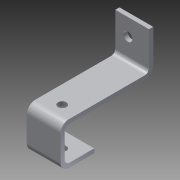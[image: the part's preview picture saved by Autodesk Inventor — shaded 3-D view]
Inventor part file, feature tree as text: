
AUTODESK INVENTOR PART (.ipt)
format: ipt  version: 2013 (Build 170138000, 138)  size: 136,704 bytes
history: native  units: in
note: dims shown in document units (in); Inventor stores cm internally (conversion verified against a paired STEP export)
features: sheet_metal_op x10, sketch x5, other x4, extrude x1, reference x1
ambient origin geometry x8: Origin, YZ Plane, XZ Plane, XY Plane, X Axis, Y Axis, Z Axis, Center Point
bodies: Solid1 (feature_tree)
feature tree (21):
  sheet_metal_op  "Face1"
  sheet_metal_op  "Flange1"
  sheet_metal_op  "Flange2"
  sheet_metal_op  "Flange3"
  extrude  "Extrusion1"  Depth=0.125in
  sketch  "Sketch1"  dims[d0=0.125in d1=0.125in]
  other  "Plate1"
  sketch  "Sketch2"  dims[d2=0.0625in]
  other  "Plate2"
  sheet_metal_op  "Bend1"
  sheet_metal_op  "Corner1"
  sketch  "Sketch3"  dims[d3=0.25in]
  other  "Plate3"
  sheet_metal_op  "Bend2"
  sheet_metal_op  "Corner2"
  sketch  "Sketch4"  dims[d4=0.125in]
  other  "Plate4"
  sheet_metal_op  "Bend3"
  sheet_metal_op  "Corner3"
  sketch  "Sketch5"  dims[d5=2.5in d6=90.0deg d7=0.125in d8=0.5in d9=0.125in d10=0.125in d11=0.125in d12=0.0625in d13=0.25in d14=0.125in d15=1.0in d16=90.0deg d17=0.125in d18=0.5in d19=0.125in d20=0.125in d21=0.125in d22=0.0625in d23=0.25in d24=0.125in d25=1.0in d26=90.0deg d27=0.125in d28=0.5in d29=0.125in d30=0.125in d31=2.1in d33=1.2784in d34=0.25in d35=1.5in d36=0.0in d37=1.0in d38=0.375in]
  reference  "Reference1"
